# Revit family: Faucet-Kitchen-KOHLER-Triton_Bowe-K-810T21
name_source: partatom
category: Plumbing Fixtures
revit_build: Autodesk Revit 2015 (Build: 20140606_1530(x64)
units: mm (PartAtom-declared; Revit-internal decimal feet)

## types (4) — shared parameters
ADA Compliant = Yes
Assembly Code = D2010
CW Connection = Yes
Cold Water Inlet = Cold Water Inlet
Date Modified = 05/29/2019
Default Elevation = 36"
Drain Included = No
Faucet Hole Spacing = 8"
Finish = Kohler-Metal-CP-Polished_Chrome
Flow Rate = 2 GPM
HW Connection = Yes
Height = 6 3/8"
Hot Water Inlet = Hot Water Inlet
Length = 8 3/16"
Manufacturer = KOHLER Co.
MasterFormat 1995 = 15410
MasterFormat 2004 = 22.41.39
Material = Brass construction
Pressure = 60.00 psi
Product Documentation Link = https://www.us.kohler.com
Product Name = Triton Bowe
Product Page URL = http://www.us.kohler.com
Spout Reach = 8 3/16"
URL = https://www.us.kohler.com
Vent Connection = No
Waste Connection = No
Waste Water Outlet = Waste Water Outlet
WaterSense Certified = No
Width = 8"

## per-type parameters (varying)
| type | Description | Lever Handle | Model | Type | Wristblade Handle |
| 1.5 GPM,Lever Handle,CP-Polished Chrome | 1.5 gpm kitchen sink faucet with 8 3/16 inch swing spout, matching finish sidespray, aerated flow and lever handles | Yes | K-810T21-4AHA-CP | 1 | No |
| 1.5 GPM,Wristblade Handle,CP-Polished Chrome | 1.5 gpm kitchen sink faucet with 8 3/16 inch swing spout, matching finish sidespray, aerated flow and wristblade handles | No | K-810T21-5AHA-CP | 2 | Yes |
| 1.8 GPM,Lever Handle,CP-Polished Chrome | 1.8 gpm kitchen sink faucet with 8 3/16 inch swing spout, matching finish sidespray, aerated flow and lever handles | Yes | K-810T21-4AFA-CP | 3 | No |
| 1.8 GPM,Wristblade Handle,CP-Polished Chrome | 1.8 gpm kitchen sink faucet with 8 3/16 inch swing spout, matching finish sidespray, aerated flow and wristblade handles | No | K-810T21-5AFA-CP | 4 | Yes |

## geometry (parser evidence)
native form markers: Sweep x7
no freeform markers — native parametric forms only
